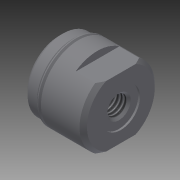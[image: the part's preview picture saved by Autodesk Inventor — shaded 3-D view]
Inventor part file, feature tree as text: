
AUTODESK INVENTOR PART (.ipt)
format: ipt  version: 2013 (Build 170138000, 138)  size: 211,968 bytes
history: native  units: in
note: dims shown in document units (in); Inventor stores cm internally (conversion verified against a paired STEP export)
features: other x112, sketch x5, revolve x2, hole x2, extrude x1
ambient origin geometry x8: Origin, YZ Plane, XZ Plane, XY Plane, X Axis, Y Axis, Z Axis, Center Point
bodies: Solid1 (feature_tree)
feature tree (122):
  revolve  "Revolution1"  [1 undecoded]
  hole  "Drilling 1"  [1 undecoded]
  hole  "Drilling 2"  [1 undecoded]
  extrude  "Extrusion1"  [1 undecoded]
  revolve  "Revolution2"  [1 undecoded]
  other  "cut1_XY"
  other  "cut1_YZ"
  other  "cut1_ZX"
  other  "cut1_X"
  other  "cut1_Y"
  other  "cut1_Z"
  other  "cut1_Center"
  other  "cut2_XY"
  other  "cut2_YZ"
  other  "cut2_ZX"
  other  "cut2_X"
  other  "cut2_Y"
  other  "cut2_Z"
  other  "cut2_Center"
  other  "to_tube_XY"
  other  "to_tube_YZ"
  other  "to_tube_ZX"
  other  "to_tube_X"
  other  "to_tube_Y"
  other  "to_tube_Z"
  other  "to_tube_Center"
  other  "lovra_XY"
  other  "lovra_YZ"
  other  "lovra_ZX"
  other  "lovra_X"
  other  "lovra_Y"
  other  "lovra_Z"
  other  "lovra_Center"
  other  "to_nut_XY"
  other  "to_nut_YZ"
  other  "to_nut_ZX"
  other  "to_nut_X"
  other  "to_nut_Y"
  other  "to_nut_Z"
  other  "to_nut_Center"
  other  "lovra1_XY"
  other  "lovra1_YZ"
  other  "lovra1_ZX"
  other  "lovra1_X"
  other  "lovra1_Y"
  other  "lovra1_Z"
  other  "lovra1_Center"
  other  "lovra2_XY"
  other  "lovra2_YZ"
  other  "lovra2_ZX"
  other  "lovra2_X"
  other  "lovra2_Y"
  other  "lovra2_Z"
  other  "lovra2_Center"
  other  "lovra3_XY"
  other  "lovra3_YZ"
  other  "lovra3_ZX"
  other  "lovra3_X"
  other  "lovra3_Y"
  other  "lovra3_Z"
  other  "lovra3_Center"
  other  "olen_XY"
  other  "olen_YZ"
  other  "olen_ZX"
  other  "olen_X"
  other  "olen_Y"
  other  "olen_Z"
  other  "olen_Center"
  other  "cutf1_XY"
  other  "cutf1_YZ"
  other  "cutf1_ZX"
  other  "cutf1_X"
  other  "cutf1_Y"
  other  "cutf1_Z"
  other  "cutf1_Center"
  other  "cutf2_XY"
  other  "cutf2_YZ"
  other  "cutf2_ZX"
  other  "cutf2_X"
  other  "cutf2_Y"
  other  "cutf2_Z"
  other  "cutf2_Center"
  other  "lovra21_XY"
  other  "lovra21_YZ"
  other  "lovra21_ZX"
  other  "lovra21_X"
  other  "lovra21_Y"
  other  "lovra21_Z"
  other  "lovra21_Center"
  other  "lovra22_XY"
  other  "lovra22_YZ"
  other  "lovra22_ZX"
  other  "lovra22_X"
  other  "lovra22_Y"
  other  "lovra22_Z"
  other  "lovra22_Center"
  other  "to_pin_XY"
  other  "to_pin_YZ"
  other  "to_pin_ZX"
  other  "to_pin_X"
  other  "to_pin_Y"
  other  "to_pin_Z"
  other  "to_pin_Center"
  other  "mbr_XY"
  other  "mbr_YZ"
  other  "mbr_ZX"
  other  "mbr_X"
  other  "mbr_Y"
  other  "mbr_Z"
  other  "mbr_Center"
  other  "to_nut1_XY"
  other  "to_nut1_YZ"
  other  "to_nut1_ZX"
  other  "to_nut1_X"
  other  "to_nut1_Y"
  other  "to_nut1_Z"
  other  "to_nut1_Center"
  sketch  "Sketch_1"  dims[d0=360.0deg]
  sketch  "Sketch2"  dims[d1=0.312in d2=0.75in d3=0.375in d4=0.25in d5=0.5635in d6=0.015in d7=0.0in]
  sketch  "Sketch3"  dims[d8=0.156in d9=0.2in d10=0.19in d11=0.25in d12=90.0deg d13=0.485in d14=0.0in d15=0.19in d16=0.0in]
  sketch  "Sketch_5"  dims[d17=360.0deg]
  sketch  "Sketch_24"
note: 5 required parameter values undecoded (feature->parameter linkage not recoverable at this tier; creation-order binding heuristic only, values carry confidence <= 0.55)